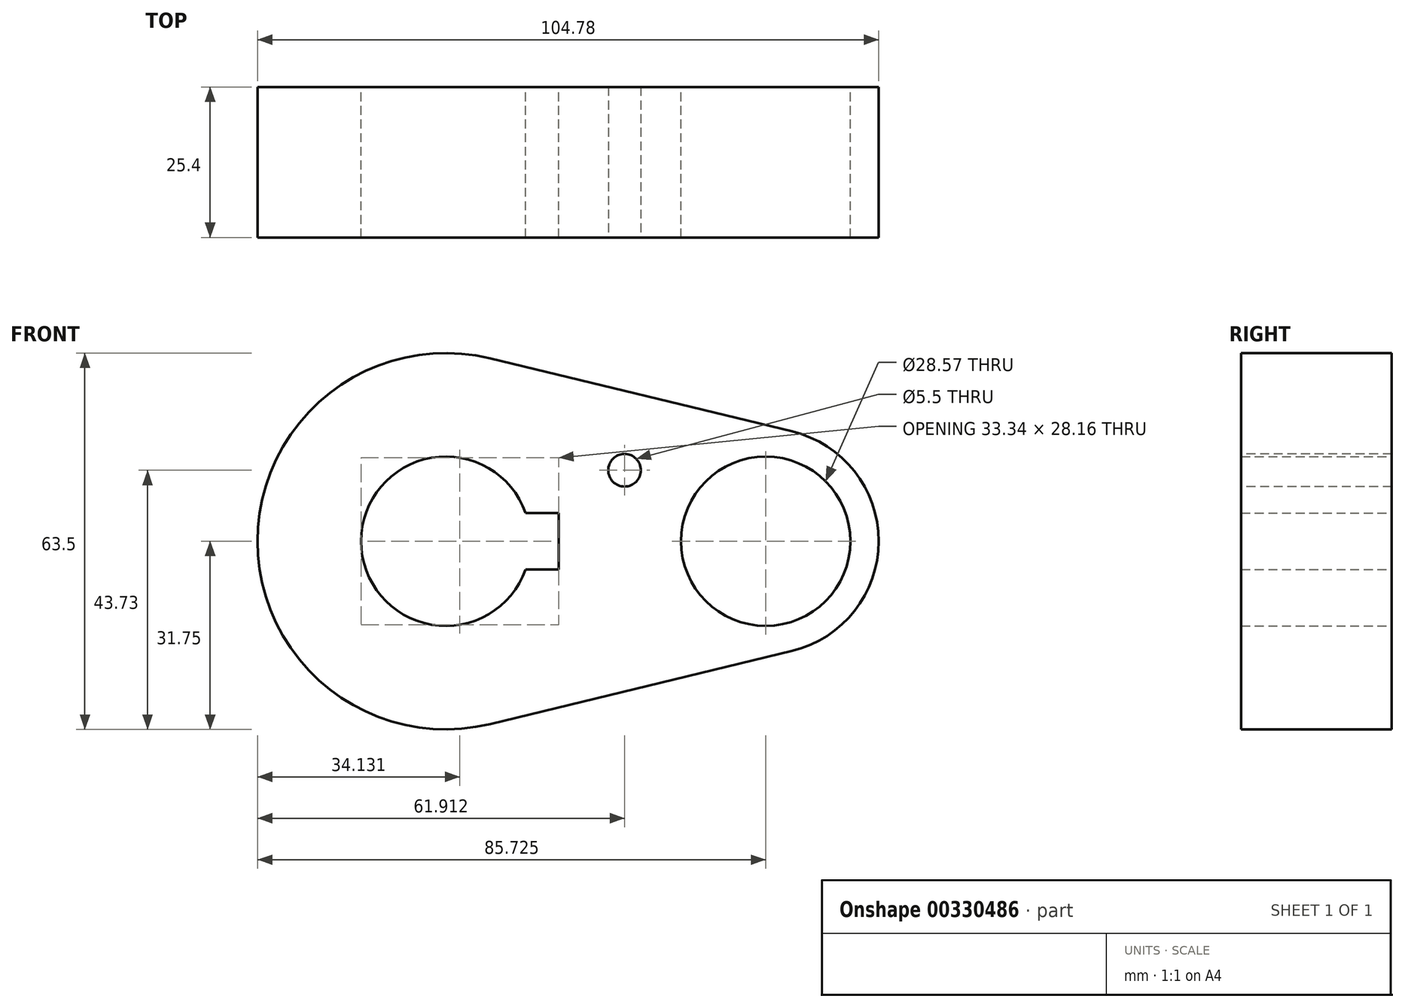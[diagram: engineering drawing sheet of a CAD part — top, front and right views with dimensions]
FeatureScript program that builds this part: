
annotation { "Feature Type Name" : "Feature", "Feature Type Description" : "" }
export const myFeature = defineFeature(function(context is Context, id is Id, definition is map)
    precondition{}
    {
        {
            var Q0;
            Q0=qCreatedBy(makeId("Front.planeOp"),FACE);
            var sketch = newSketch(context, id + "F0", { "sketchPlane" : qUnion([Q0])});
            skCircle(sketch, "E0", {"center": v(0, 0) * mm, "radius": 31.75 * mm});
            skCircle(sketch, "E1", {"center": v(53.98, 0) * mm, "radius": 19.05 * mm});
            skLineSegment(sketch, "E2", {"start": v(7.47, 30.86) * mm, "end": v(58.46, 18.52) * mm});
            skLineSegment(sketch, "E3", {"start": v(7.47, -30.86) * mm, "end": v(58.46, -18.52) * mm});
            skCircle(sketch, "E4", {"center": v(0, 0) * mm, "radius": 14.29 * mm});
            skCircle(sketch, "E5", {"center": v(53.98, 0) * mm, "radius": 14.29 * mm});
            skLineSegment(sketch, "E6.bottom", {"start": v(19.05, -4.76) * mm, "end": v(-19.05, -4.76) * mm});
            skLineSegment(sketch, "E6.top", {"start": v(19.05, 4.76) * mm, "end": v(-19.05, 4.76) * mm});
            skLineSegment(sketch, "E6.left", {"start": v(19.05, -4.76) * mm, "end": v(19.05, 4.76) * mm});
            skLineSegment(sketch, "E6.right", {"start": v(-19.05, -4.76) * mm, "end": v(-19.05, 4.76) * mm});
            skSolve(sketch);
        }
        {
            var Q0;
            {var subQ7=sQuery(id+"F0.wireOp",EDGE,"E6.left");Q0=makeQuery(id+"F0.imprint","IMPRINT",FACE,{"disambiguationData":[TD([[makeQuery(id+"F0.imprint","IMPRINT",EDGE,{"derivedFrom":subQ7}),-1.0]])]});}
            var Q1;
            {var subQ5=sQuery(id+"F0.wireOp",EDGE,"E6.right");Q1=makeQuery(id+"F0.imprint","IMPRINT",FACE,{"disambiguationData":[TD([[makeQuery(id+"F0.imprint","IMPRINT",EDGE,{"derivedFrom":subQ5}),-1.0]])]});}
            var Q2;
            {var subQ0=sQuery(id+"F0.wireOp",EDGE,"E2");Q2=makeQuery(id+"F0.imprint","IMPRINT",FACE,{"disambiguationData":[TD([[makeQuery(id+"F0.imprint","IMPRINT",EDGE,{"derivedFrom":subQ0}),-1.0]])]});}
            var Q3;
            Q3=makeQuery(id+"F0.imprint","IMPRINT",FACE,{"disambiguationData":[TD([[makeQuery(id+"F0.imprint","IMPRINT",EDGE,{"derivedFrom":sQuery(id+"F0.wireOp",EDGE,"E5")}),-1.0]])]});
            extrude(context, id + "F1", {"entities" : qUnion([Q0, Q1, Q2, Q3]), "depth" : 25.4 * mm});
        }
        {
            var Q0;
            Q0=makeQuery(id+"F1.opExtrude","CAP_FACE",FACE,{"disambiguationData":[OSD([sQuery(id+"F0.wireOp",EDGE,"E0"),sQuery(id+"F0.wireOp",EDGE,"E1"),sQuery(id+"F0.wireOp",EDGE,"E2"),sQuery(id+"F0.wireOp",EDGE,"E3"),sQuery(id+"F0.wireOp",EDGE,"E4"),sQuery(id+"F0.wireOp",EDGE,"E5"),sQuery(id+"F0.wireOp",EDGE,"E6.bottom"),sQuery(id+"F0.wireOp",EDGE,"E6.top"),sQuery(id+"F0.wireOp",EDGE,"E6.left")])],"isStart":false});
            var sketch = newSketch(context, id + "F2", { "sketchPlane" : qUnion([Q0])});
            skPoint(sketch, "E7", {"position": v(30.16, 11.98) * mm});
            skSolve(sketch);
        }
        {
            var Q0;
            Q0=sQuery(id+"F2.wireOp",VERTEX,"E7");
            var Q1;
            Q1=makeQuery(id+"F1.opExtrude","SWEPT_BODY",BODY,{"disambiguationData":[OSD([sQuery(id+"F0.wireOp",EDGE,"E0"),sQuery(id+"F0.wireOp",EDGE,"E1"),sQuery(id+"F0.wireOp",EDGE,"E2"),sQuery(id+"F0.wireOp",EDGE,"E3"),sQuery(id+"F0.wireOp",EDGE,"E4"),sQuery(id+"F0.wireOp",EDGE,"E5"),sQuery(id+"F0.wireOp",EDGE,"E6.bottom"),sQuery(id+"F0.wireOp",EDGE,"E6.top"),sQuery(id+"F0.wireOp",EDGE,"E6.left")])]});
            hole(context, id + "F3", {"style" : HoleStyle.SIMPLE, "endStyle" : HoleEndStyle.THROUGH, "standardTappedOrClearance" : lookupTablePath({ "standard" : "ISO", "fit" : "Normal", "size" : "M5", "type" : "Clearance" }), "standardBlindInLast" : lookupTablePath({ "fit" : "Standard", "standard" : "ISO", "size" : "M5", "type" : "Clearance" }), "holeDiameter" : 5.5 * mm, "tappedDepth" : 12 * mm, "tapClearance" : 3, "locations" : qUnion([Q0]), "scope" : qUnion([Q1])});
        }
    });
